# Revit family: Accessory-Controller_Module-KOHLER-DTV-K-99695_1
name_source: partatom
category: Electrical Fixtures
revit_build: Autodesk Revit 2015 (Build: 20140606_1530(x64)
units: mm (PartAtom-declared; Revit-internal decimal feet)

## types (2) — shared parameters
ADA Compliant = No
Apparent Load = 1800 VA
Assembly Code = D5010
Date Modified = 04/29/2019
Default Elevation = 42"
Electrical Connector = Yes
Electrical Note = One dedicated circuit required, protected with Class A Ground-Fault Circuit-Interrupter (GFCI) or Residual Current Device (RCD)
Finish = Kohler-Plastic-7-Black_Black
Height = 1 3/4"
Length = 9 1/2"
Manufacturer = KOHLER Co.
MasterFormat 1995 = 10820
MasterFormat 2004 = 10.28.13
Material = Thermoplastic Casing
Product Documentation Link = https://www.us.kohler.com
Product Name = DTV+
Product Page URL = http://www.us.kohler.com
URL = https://www.us.kohler.com
Voltage = 120 V
WaterSense Certified = No
Width = 5 3/8"

## per-type parameters (varying)
| type | Description | Model | Type |
| Eco system controller, NA-Not Applicable | Eco system controller module | K-99695-E-NA | 2 |
| System controller, NA-Not Applicable | System controller module | K-99695-NA | 1 |

## geometry (parser evidence)
native form markers: Sweep x5
no freeform markers — native parametric forms only
